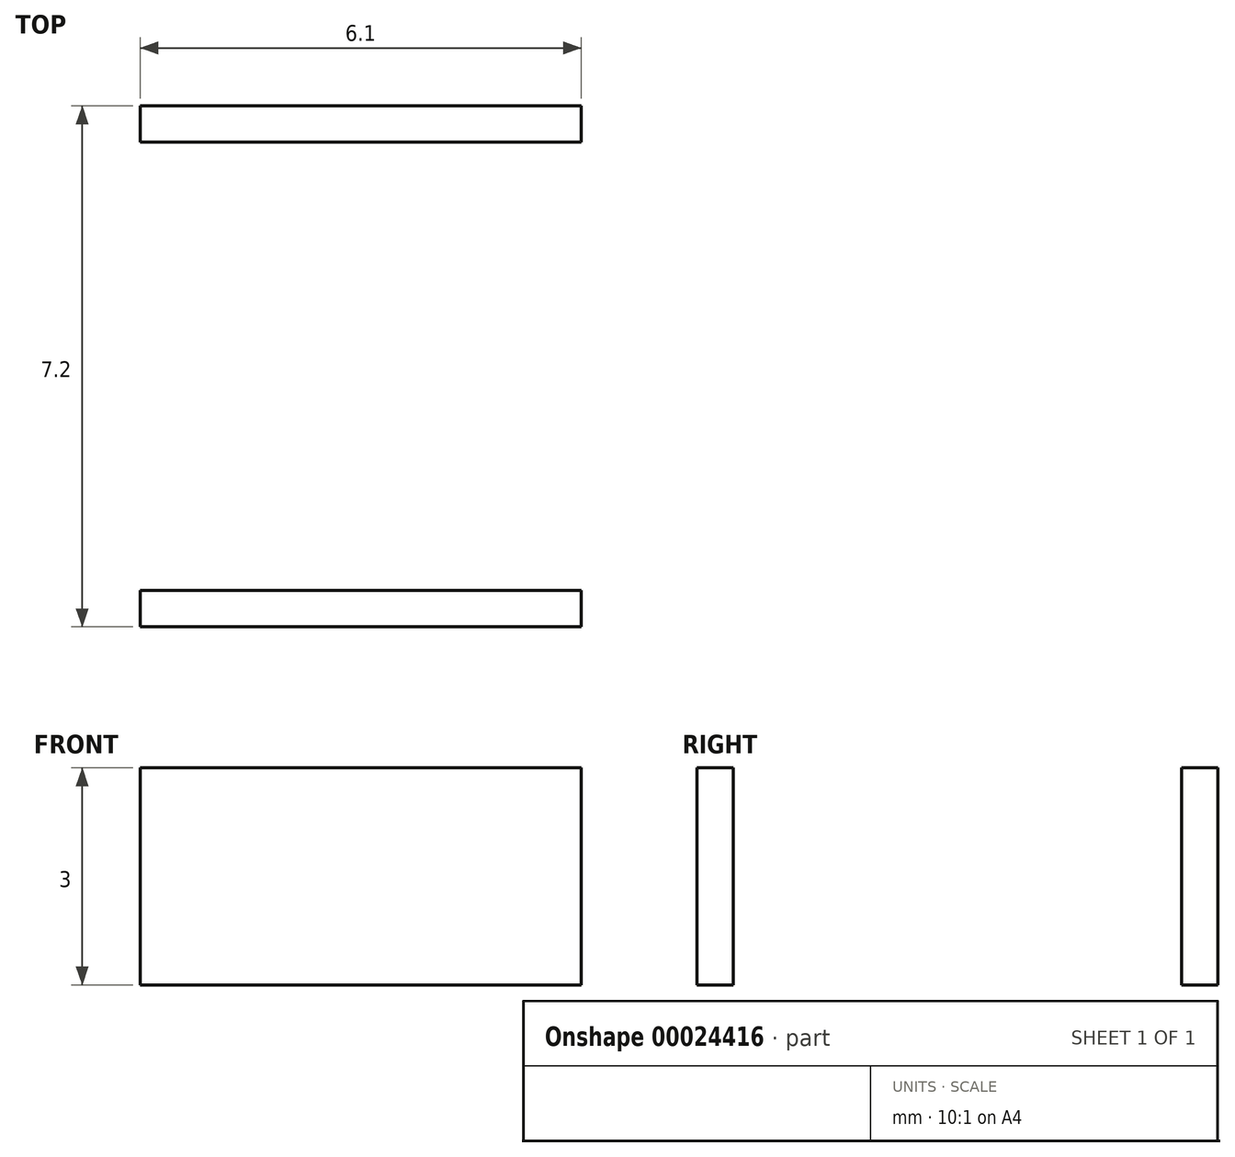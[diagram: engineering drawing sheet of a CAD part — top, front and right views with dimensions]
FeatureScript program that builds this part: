
annotation { "Feature Type Name" : "Feature", "Feature Type Description" : "" }
export const myFeature = defineFeature(function(context is Context, id is Id, definition is map)
    precondition{}
    {
        {
            var Q0;
            Q0=qCreatedBy(makeId("Top.planeOp"),FACE);
            var sketch = newSketch(context, id + "F0", { "sketchPlane" : qUnion([Q0])});
            skLineSegment(sketch, "E0.rect.bottom", {"start": v(3.05, -3.6) * mm, "end": v(-3.05, -3.6) * mm});
            skLineSegment(sketch, "E0.rect.top", {"start": v(3.05, 3.6) * mm, "end": v(-3.05, 3.6) * mm});
            skLineSegment(sketch, "E0.rect.left", {"start": v(3.05, -3.6) * mm, "end": v(3.05, 3.6) * mm});
            skLineSegment(sketch, "E0.rect.right", {"start": v(-3.05, -3.6) * mm, "end": v(-3.05, 3.6) * mm});
            skPoint(sketch, "E0.rect.middle", {"position": v(0, 0) * mm});
            skLineSegment(sketch, "E1.rect.bottom", {"start": v(3.05, -3.1) * mm, "end": v(-3.05, -3.1) * mm});
            skLineSegment(sketch, "E1.rect.top", {"start": v(3.05, 3.1) * mm, "end": v(-3.05, 3.1) * mm});
            skLineSegment(sketch, "E1.rect.left", {"start": v(3.05, -3.1) * mm, "end": v(3.05, 3.1) * mm});
            skLineSegment(sketch, "E1.rect.right", {"start": v(-3.05, -3.1) * mm, "end": v(-3.05, 3.1) * mm});
            skSolve(sketch);
        }
        {
            var Q0;
            Q0=makeQuery(id+"F0.imprint","IMPRINT",FACE,{"disambiguationData":[TD([[makeQuery(id+"F0.imprint","IMPRINT",EDGE,{"derivedFrom":sQuery(id+"F0.wireOp",EDGE,"E1.rect.bottom")}),-1.0]])]});
            extrude(context, id + "F1", {"entities" : qUnion([Q0]), "depth" : 3 * mm});
        }
        {
            var Q0;
            {var subQ2=sQuery(id+"F0.wireOp",EDGE,"E0.rect.bottom");Q0=makeQuery(id+"F0.imprint","IMPRINT",FACE,{"disambiguationData":[TD([[makeQuery(id+"F0.imprint","IMPRINT",EDGE,{"derivedFrom":subQ2}),-1.0]])]});}
            var Q1;
            {var subQ2=sQuery(id+"F0.wireOp",EDGE,"E0.rect.top");Q1=makeQuery(id+"F0.imprint","IMPRINT",FACE,{"disambiguationData":[TD([[makeQuery(id+"F0.imprint","IMPRINT",EDGE,{"derivedFrom":subQ2}),1.0]])]});}
            extrude(context, id + "F2", {"entities" : qUnion([Q0, Q1]), "depth" : 3 * mm});
        }
        {
            var Q0;
            Q0=makeQuery(id+"F1.opExtrude","SWEPT_BODY",BODY,{"disambiguationData":[OSD([sQuery(id+"F0.wireOp",EDGE,"E1.rect.bottom"),sQuery(id+"F0.wireOp",EDGE,"E1.rect.top"),sQuery(id+"F0.wireOp",EDGE,"E1.rect.left"),sQuery(id+"F0.wireOp",EDGE,"E1.rect.right")])]});
            deleteBodies(context, id + "F3", {"entities" : qUnion([Q0])});
        }
    });
